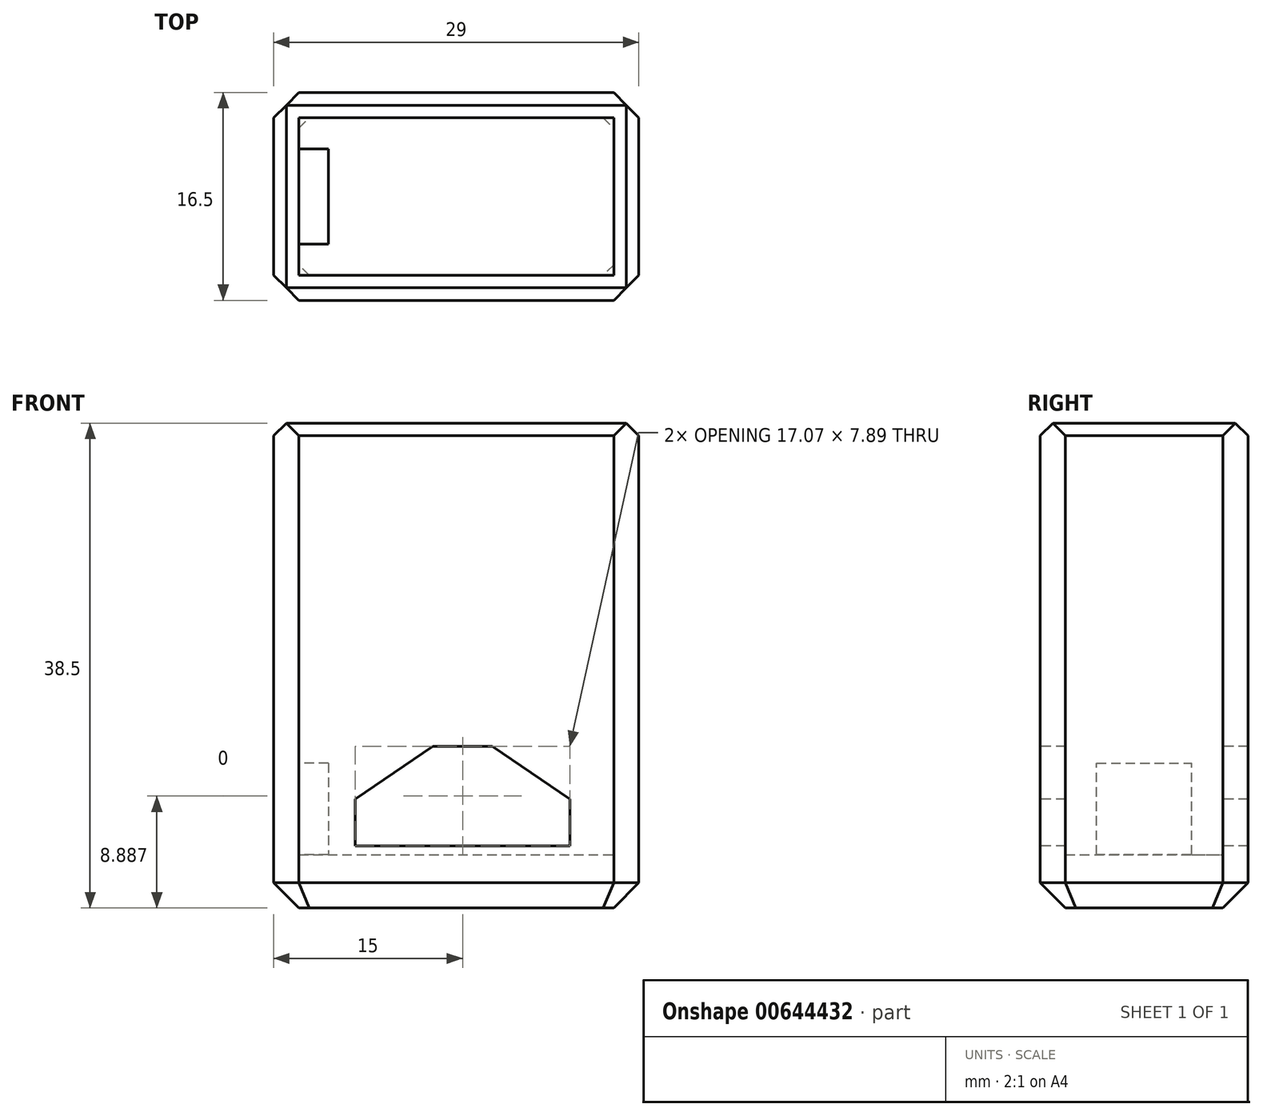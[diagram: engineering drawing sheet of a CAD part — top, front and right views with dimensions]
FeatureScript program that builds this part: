
annotation { "Feature Type Name" : "Feature", "Feature Type Description" : "" }
export const myFeature = defineFeature(function(context is Context, id is Id, definition is map)
    precondition{}
    {
        {
            var Q0;
            Q0=qCreatedBy(makeId("Top.planeOp"),FACE);
            var sketch = newSketch(context, id + "F0", { "sketchPlane" : qUnion([Q0])});
            skLineSegment(sketch, "E0.bottom", {"start": v(0, 0) * mm, "end": v(29, 0) * mm});
            skLineSegment(sketch, "E0.top", {"start": v(0, 16.5) * mm, "end": v(29, 16.5) * mm});
            skLineSegment(sketch, "E0.left", {"start": v(0, 0) * mm, "end": v(0, 16.5) * mm});
            skLineSegment(sketch, "E0.right", {"start": v(29, 0) * mm, "end": v(29, 16.5) * mm});
            skSolve(sketch);
        }
        {
            var Q0;
            Q0=makeQuery(id+"F0.imprint","IMPRINT",FACE,{"disambiguationData":[TD([[makeQuery(id+"F0.imprint","IMPRINT",EDGE,{"derivedFrom":sQuery(id+"F0.wireOp",EDGE,"E0.bottom")}),1.0]])]});
            extrude(context, id + "F1", {"entities" : qUnion([Q0]), "oppositeDirection" : true, "depth" : 38.5 * mm, "offsetDistance" : 25 * mm});
        }
        {
            var Q0;
            Q0=makeQuery(id+"F1.opExtrude","CAP_FACE",FACE,{"disambiguationData":[OSD([sQuery(id+"F0.wireOp",EDGE,"E0.bottom"),sQuery(id+"F0.wireOp",EDGE,"E0.top"),sQuery(id+"F0.wireOp",EDGE,"E0.left"),sQuery(id+"F0.wireOp",EDGE,"E0.right")])],"isStart":true});
            shell(context, id + "F2", {"entities" : qUnion([Q0]), "thickness" : 2 * mm});
        }
        {
            var Q0;
            Q0=makeQuery(id+"F2.opShell","OFFSET_FACE",FACE,{"disambiguationData":[OSD([sQuery(id+"F0.wireOp",EDGE,"E0.bottom"),sQuery(id+"F0.wireOp",EDGE,"E0.top"),sQuery(id+"F0.wireOp",EDGE,"E0.left"),sQuery(id+"F0.wireOp",EDGE,"E0.right")])]});
            extrude(context, id + "F3", {"entities" : qUnion([Q0]), "operationType" : NewBodyOperationType.ADD, "depth" : 2.25 * mm, "offsetDistance" : 25 * mm});
        }
        {
            var Q0;
            Q0=makeQuery(id+"F1.opExtrude","SWEPT_EDGE",EDGE,{"disambiguationData":[OSD([sQuery(id+"F0.wireOp",EDGE,"E0.bottom"),sQuery(id+"F0.wireOp",EDGE,"E0.right")])]});
            var Q1;
            Q1=makeQuery(id+"F1.opExtrude","SWEPT_EDGE",EDGE,{"disambiguationData":[OSD([sQuery(id+"F0.wireOp",EDGE,"E0.bottom"),sQuery(id+"F0.wireOp",EDGE,"E0.left")])]});
            var Q2;
            Q2=makeQuery(id+"F1.opExtrude","SWEPT_EDGE",EDGE,{"disambiguationData":[OSD([sQuery(id+"F0.wireOp",EDGE,"E0.top"),sQuery(id+"F0.wireOp",EDGE,"E0.left")])]});
            var Q3;
            Q3=makeQuery(id+"F1.opExtrude","SWEPT_EDGE",EDGE,{"disambiguationData":[OSD([sQuery(id+"F0.wireOp",EDGE,"E0.top"),sQuery(id+"F0.wireOp",EDGE,"E0.right")])]});
            chamfer(context, id + "F4", {"entities" : qUnion([Q0, Q1, Q2, Q3]), "width" : 2 * mm, "tangentPropagation" : true});
        }
        {
            var Q0;
            Q0=makeQuery(id+"F1.opExtrude","CAP_FACE",FACE,{"disambiguationData":[OSD([sQuery(id+"F0.wireOp",EDGE,"E0.bottom"),sQuery(id+"F0.wireOp",EDGE,"E0.top"),sQuery(id+"F0.wireOp",EDGE,"E0.left"),sQuery(id+"F0.wireOp",EDGE,"E0.right")])],"isStart":false});
            chamfer(context, id + "F5", {"entities" : qUnion([Q0]), "width" : 2 * mm, "tangentPropagation" : true});
        }
        {
            var Q0;
            Q0=makeQuery(id+"F1.opExtrude","CAP_EDGE",EDGE,{"disambiguationData":[OSD([sQuery(id+"F0.wireOp",EDGE,"E0.left")])],"isStart":true});
            var Q1;
            Q1=makeQuery(id+"F1.opExtrude","CAP_EDGE",EDGE,{"disambiguationData":[OSD([sQuery(id+"F0.wireOp",EDGE,"E0.top")])],"isStart":true});
            var Q2;
            Q2=makeQuery(id+"F1.opExtrude","CAP_EDGE",EDGE,{"disambiguationData":[OSD([sQuery(id+"F0.wireOp",EDGE,"E0.right")])],"isStart":true});
            var Q3;
            Q3=makeQuery(id+"F1.opExtrude","CAP_EDGE",EDGE,{"disambiguationData":[OSD([sQuery(id+"F0.wireOp",EDGE,"E0.bottom")])],"isStart":true});
            chamfer(context, id + "F6", {"entities" : qUnion([Q0, Q1, Q2, Q3]), "width" : 1 * mm, "tangentPropagation" : true});
        }
        {
            var Q0;
            Q0=makeQuery(id+"F1.opExtrude","SWEPT_FACE",FACE,{"disambiguationData":[OSD([sQuery(id+"F0.wireOp",EDGE,"E0.bottom")])]});
            var sketch = newSketch(context, id + "F7", { "sketchPlane" : qUnion([Q0])});
            skLineSegment(sketch, "E1", {"start": v(23.54, -29.84) * mm, "end": v(23.54, -33.56) * mm});
            skLineSegment(sketch, "E2", {"start": v(23.54, -33.56) * mm, "end": v(6.46, -33.56) * mm});
            skLineSegment(sketch, "E3", {"start": v(6.46, -33.56) * mm, "end": v(6.46, -29.84) * mm});
            skLineSegment(sketch, "E4", {"start": v(6.46, -29.84) * mm, "end": v(12.63, -25.67) * mm});
            skLineSegment(sketch, "E5", {"start": v(12.63, -25.67) * mm, "end": v(17.36, -25.67) * mm});
            skLineSegment(sketch, "E6", {"start": v(17.36, -25.67) * mm, "end": v(23.54, -29.84) * mm});
            skSolve(sketch);
        }
        {
            var Q0;
            Q0 = qSketchRegion(id + "F7", true);
            extrude(context, id + "F8", {"entities" : qUnion([Q0]), "operationType" : NewBodyOperationType.REMOVE, "endBound" : BoundingType.THROUGH_ALL, "oppositeDirection" : true, "depth" : 25 * mm, "offsetDistance" : 25 * mm});
        }
        {
            var Q0;
            Q0=makeQuery(id+"F1.opExtrude","SWEPT_FACE",FACE,{"disambiguationData":[OSD([sQuery(id+"F0.wireOp",EDGE,"E0.left")])]});
            var sketch = newSketch(context, id + "F9", { "sketchPlane" : qUnion([Q0])});
            skLineSegment(sketch, "E7.bottom", {"start": v(-12.02, -27) * mm, "end": v(-4.48, -27) * mm});
            skLineSegment(sketch, "E7.top", {"start": v(-12.02, -34.25) * mm, "end": v(-4.48, -34.25) * mm});
            skLineSegment(sketch, "E7.left", {"start": v(-12.02, -27) * mm, "end": v(-12.02, -34.25) * mm});
            skLineSegment(sketch, "E7.right", {"start": v(-4.48, -27) * mm, "end": v(-4.48, -34.25) * mm});
            skCircle(sketch, "E8", {"center": v(-8.25, -29.5) * mm, "radius": 1.1 * mm});
            skSolve(sketch);
        }
        {
            var Q0;
            Q0=makeQuery(id+"F9.imprint","IMPRINT",FACE,{"disambiguationData":[TD([[makeQuery(id+"F9.imprint","IMPRINT",EDGE,{"derivedFrom":sQuery(id+"F9.wireOp",EDGE,"E8")}),1.0]])]});
            var Q1;
            Q1=makeQuery(id+"F9.imprint","IMPRINT",FACE,{"disambiguationData":[TD([[makeQuery(id+"F9.imprint","IMPRINT",EDGE,{"derivedFrom":sQuery(id+"F9.wireOp",EDGE,"E7.bottom")}),-1.0]])]});
            extrude(context, id + "F10", {"entities" : qUnion([Q0, Q1]), "operationType" : NewBodyOperationType.ADD, "oppositeDirection" : true, "depth" : 4.35 * mm, "offsetDistance" : 25 * mm});
        }
    });
